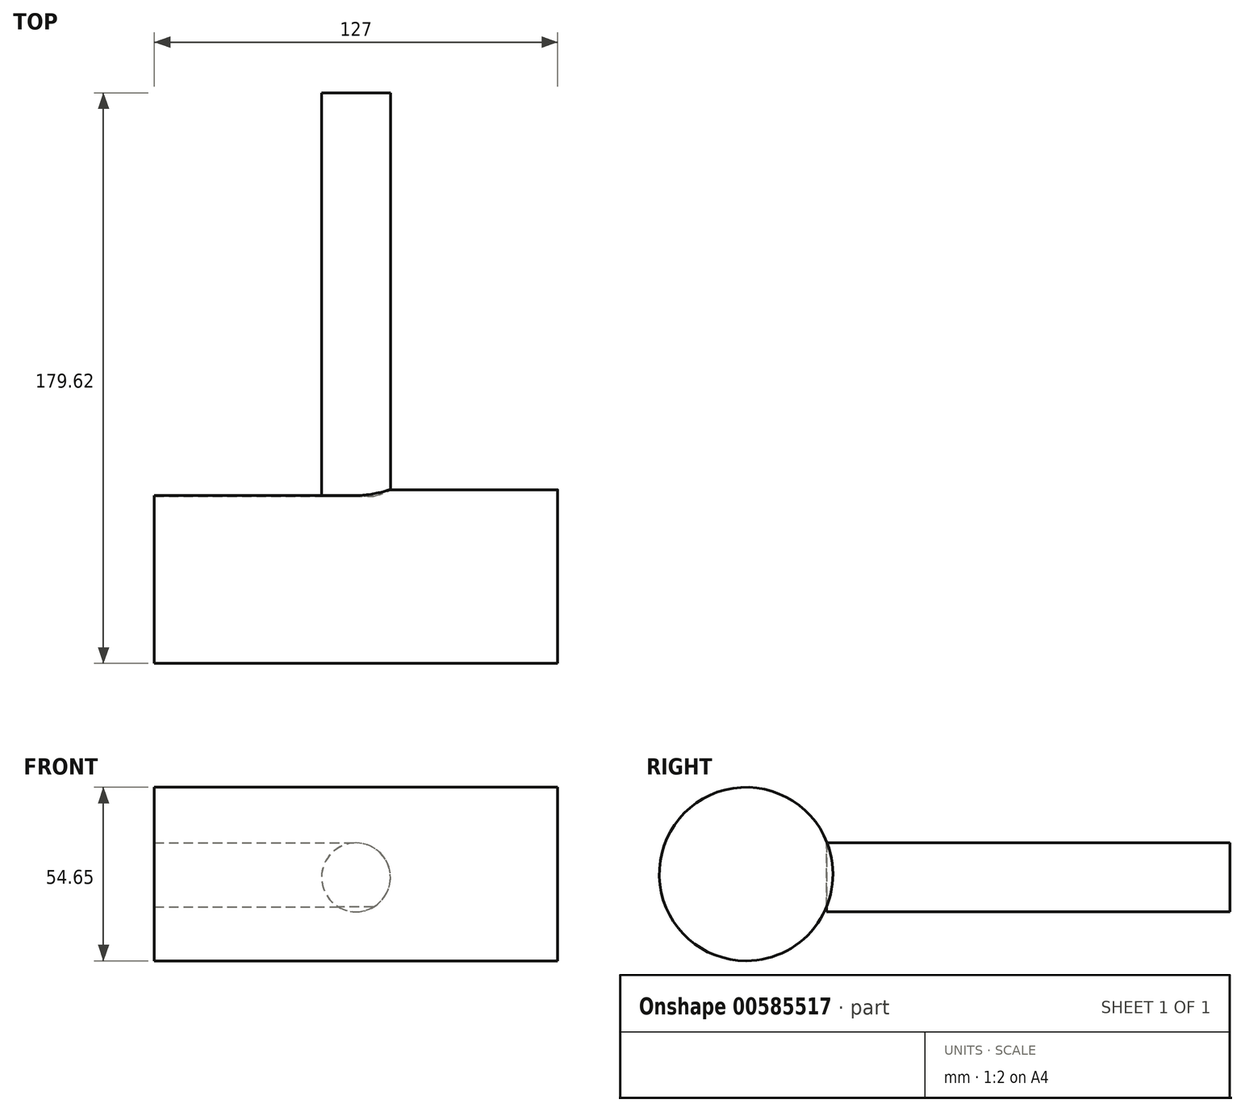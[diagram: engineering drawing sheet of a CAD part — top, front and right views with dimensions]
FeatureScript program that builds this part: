
annotation { "Feature Type Name" : "Feature", "Feature Type Description" : "" }
export const myFeature = defineFeature(function(context is Context, id is Id, definition is map)
    precondition{}
    {
        {
            var Q0;
            Q0=qCreatedBy(makeId("Front.planeOp"),FACE);
            var sketch = newSketch(context, id + "F0", { "sketchPlane" : qUnion([Q0])});
            skCircle(sketch, "E0", {"center": v(0, 0) * mm, "radius": 10.84 * mm});
            skSolve(sketch);
        }
        {
            var Q0;
            Q0=makeQuery(id+"F0.imprint","IMPRINT",FACE,{"disambiguationData":[TD([[makeQuery(id+"F0.imprint","IMPRINT",EDGE,{"derivedFrom":sQuery(id+"F0.wireOp",EDGE,"E0")}),1.0]])]});
            extrude(context, id + "F1", {"entities" : qUnion([Q0]), "depth" : 50.8 * mm, "offsetDistance" : 25.4 * mm});
        }
        {
            var Q0;
            Q0=makeQuery(id+"F1.opExtrude","CAP_FACE",FACE,{"disambiguationData":[OSD([sQuery(id+"F0.wireOp",EDGE,"E0")])],"isStart":false});
            extrude(context, id + "F2", {"entities" : qUnion([Q0]), "operationType" : NewBodyOperationType.ADD, "depth" : 76.2 * mm, "offsetDistance" : 25.4 * mm});
        }
        {
            var Q0;
            Q0=qCreatedBy(makeId("Right.planeOp"),FACE);
            var sketch = newSketch(context, id + "F3", { "sketchPlane" : qUnion([Q0])});
            skCircle(sketch, "E1", {"center": v(-152.29, 1.04) * mm, "radius": 27.33 * mm});
            skPoint(sketch, "E1.first.point", {"position": v(-124.98, 0) * mm});
            skPoint(sketch, "E1.second.point", {"position": v(-179.6, 0) * mm});
            skPoint(sketch, "E1.third.point", {"position": v(-174.82, -14.42) * mm});
            skSolve(sketch);
        }
        {
            var Q0;
            Q0=makeQuery(id+"F3.imprint","IMPRINT",FACE,{"disambiguationData":[TD([[makeQuery(id+"F3.imprint","IMPRINT",EDGE,{"derivedFrom":sQuery(id+"F3.wireOp",EDGE,"E1")}),1.0]])]});
            extrude(context, id + "F4", {"entities" : qUnion([Q0]), "operationType" : NewBodyOperationType.ADD, "depth" : 63.5 * mm, "offsetDistance" : 25.4 * mm});
        }
        {
            var Q0;
            Q0=makeQuery(id+"F4.opExtrude","CAP_FACE",FACE,{"disambiguationData":[OSD([sQuery(id+"F3.wireOp",EDGE,"E1")])],"isStart":true});
            extrude(context, id + "F5", {"entities" : qUnion([Q0]), "operationType" : NewBodyOperationType.ADD, "depth" : 63.5 * mm, "offsetDistance" : 25.4 * mm});
        }
    });
